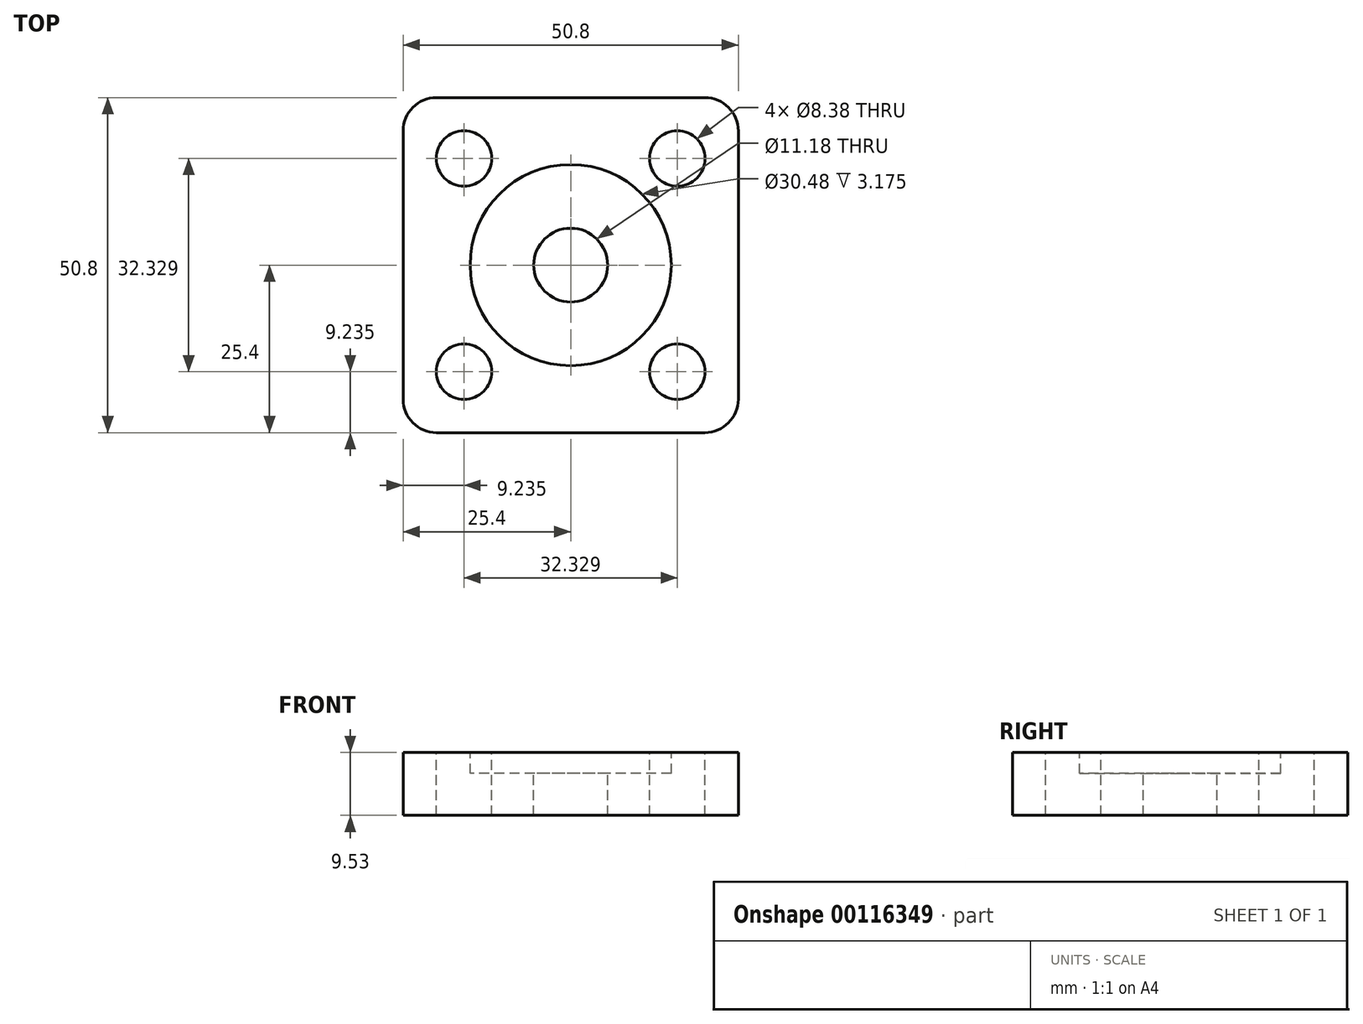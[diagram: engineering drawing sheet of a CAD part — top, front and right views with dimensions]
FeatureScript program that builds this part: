
annotation { "Feature Type Name" : "Feature", "Feature Type Description" : "" }
export const myFeature = defineFeature(function(context is Context, id is Id, definition is map)
    precondition{}
    {
        {
            var Q0;
            Q0=qCreatedBy(makeId("Top.planeOp"),FACE);
            var sketch = newSketch(context, id + "F0", { "sketchPlane" : qUnion([Q0])});
            skLineSegment(sketch, "E0.bottom", {"start": v(25.4, -25.4) * mm, "end": v(-25.4, -25.4) * mm});
            skLineSegment(sketch, "E0.top", {"start": v(25.4, 25.4) * mm, "end": v(-25.4, 25.4) * mm});
            skLineSegment(sketch, "E0.left", {"start": v(25.4, -25.4) * mm, "end": v(25.4, 25.4) * mm});
            skLineSegment(sketch, "E0.right", {"start": v(-25.4, -25.4) * mm, "end": v(-25.4, 25.4) * mm});
            skPoint(sketch, "E0.middle", {"position": v(0, 0) * mm});
            skCircle(sketch, "E1", {"center": v(0, 0) * mm, "radius": 15.24 * mm});
            skCircle(sketch, "E2", {"center": v(0, 0) * mm, "radius": 22.86 * mm});
            skLineSegment(sketch, "E3", {"start": v(0, 0) * mm, "end": v(25.4, 25.4) * mm});
            skCircle(sketch, "E4", {"center": v(16.16, 16.16) * mm, "radius": 4.2 * mm});
            skCircle(sketch, "E5.1.0", {"center": v(-16.16, 16.16) * mm, "radius": 4.2 * mm});
            skCircle(sketch, "E5.2.0", {"center": v(-16.16, -16.16) * mm, "radius": 4.2 * mm});
            skCircle(sketch, "E5.3.0", {"center": v(16.16, -16.16) * mm, "radius": 4.2 * mm});
            skCircle(sketch, "E6", {"center": v(0, 0) * mm, "radius": 5.59 * mm});
            skSolve(sketch);
        }
        {
            var Q0;
            Q0=makeQuery(id+"F0.imprint","IMPRINT",FACE,{"disambiguationData":[TD([[makeQuery(id+"F0.imprint","IMPRINT",EDGE,{"derivedFrom":sQuery(id+"F0.wireOp",EDGE,"E0.bottom")}),-1.0]])]});
            var Q1;
            Q1=makeQuery(id+"F0.imprint","IMPRINT",FACE,{"disambiguationData":[TD([[makeQuery(id+"F0.imprint","IMPRINT",EDGE,{"derivedFrom":sQuery(id+"F0.wireOp",EDGE,"E1")}),-1.0]])]});
            var Q2;
            Q2=makeQuery(id+"F0.imprint","IMPRINT",FACE,{"disambiguationData":[TD([[makeQuery(id+"F0.imprint","IMPRINT",EDGE,{"derivedFrom":sQuery(id+"F0.wireOp",EDGE,"E1")}),1.0]])]});
            extrude(context, id + "F1", {"entities" : qUnion([Q0, Q1, Q2]), "oppositeDirection" : true, "depth" : 9.52 * mm});
        }
        {
            var Q0;
            Q0=makeQuery(id+"F0.imprint","IMPRINT",FACE,{"disambiguationData":[TD([[makeQuery(id+"F0.imprint","IMPRINT",EDGE,{"derivedFrom":sQuery(id+"F0.wireOp",EDGE,"E1")}),1.0]])]});
            extrude(context, id + "F2", {"entities" : qUnion([Q0]), "operationType" : NewBodyOperationType.REMOVE, "oppositeDirection" : true, "depth" : 3.17 * mm});
        }
        {
            var Q0;
            Q0=makeQuery(id+"F1.opExtrude","SWEPT_EDGE",EDGE,{"disambiguationData":[OSD([sQuery(id+"F0.wireOp",EDGE,"E0.bottom"),sQuery(id+"F0.wireOp",EDGE,"E0.right")])]});
            var Q1;
            Q1=makeQuery(id+"F1.opExtrude","SWEPT_EDGE",EDGE,{"disambiguationData":[OSD([sQuery(id+"F0.wireOp",EDGE,"E0.bottom"),sQuery(id+"F0.wireOp",EDGE,"E0.left")])]});
            var Q2;
            Q2=makeQuery(id+"F1.opExtrude","SWEPT_EDGE",EDGE,{"disambiguationData":[OSD([sQuery(id+"F0.wireOp",EDGE,"E0.top"),sQuery(id+"F0.wireOp",EDGE,"E0.left")])]});
            var Q3;
            Q3=makeQuery(id+"F1.opExtrude","SWEPT_EDGE",EDGE,{"disambiguationData":[OSD([sQuery(id+"F0.wireOp",EDGE,"E0.top"),sQuery(id+"F0.wireOp",EDGE,"E0.right")])]});
            fillet(context, id + "F3", {"entities" : qUnion([Q0, Q1, Q2, Q3]), "radius" : 5.08 * mm, "tangentPropagation" : true, "allowEdgeOverflow" : false});
        }
    });
